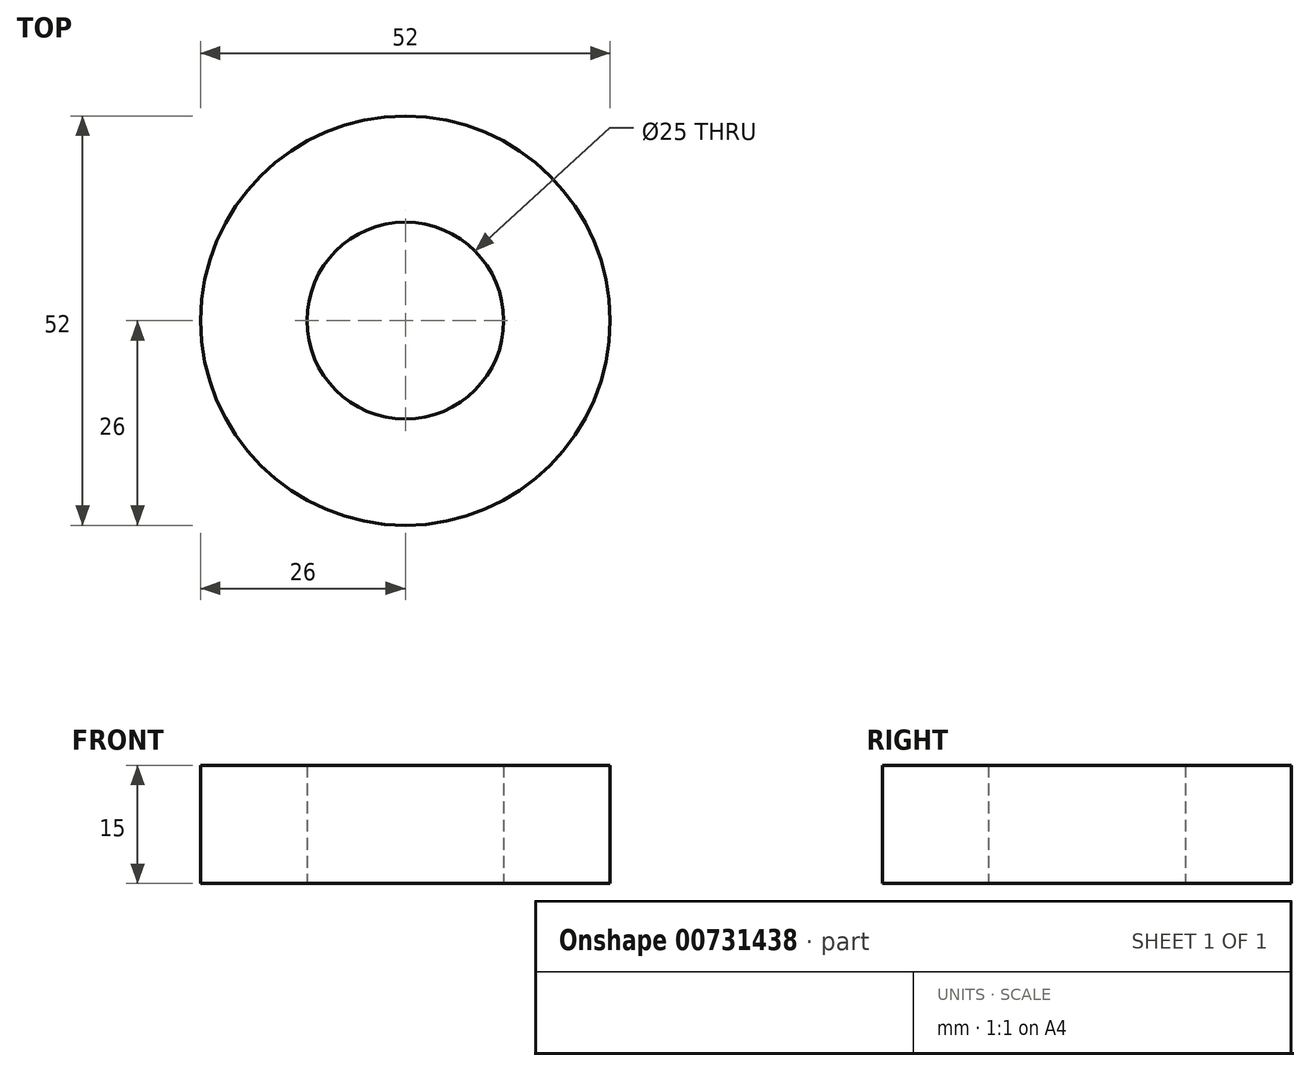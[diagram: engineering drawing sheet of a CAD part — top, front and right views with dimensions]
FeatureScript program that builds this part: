
annotation { "Feature Type Name" : "Feature", "Feature Type Description" : "" }
export const myFeature = defineFeature(function(context is Context, id is Id, definition is map)
    precondition{}
    {
        {
            var Q0;
            Q0=qCreatedBy(makeId("Top.planeOp"),FACE);
            var sketch = newSketch(context, id + "F0", { "sketchPlane" : qUnion([Q0])});
            skCircle(sketch, "E0", {"center": v(0, 0) * mm, "radius": 12.5 * mm});
            skCircle(sketch, "E1", {"center": v(0, 0) * mm, "radius": 26 * mm});
            skSolve(sketch);
        }
        {
            var Q0;
            Q0 = qSketchRegion(id + "F0", true);
            extrude(context, id + "F1", {"entities" : qUnion([Q0]), "depth" : 15 * mm, "offsetDistance" : 25 * mm});
        }
    });
